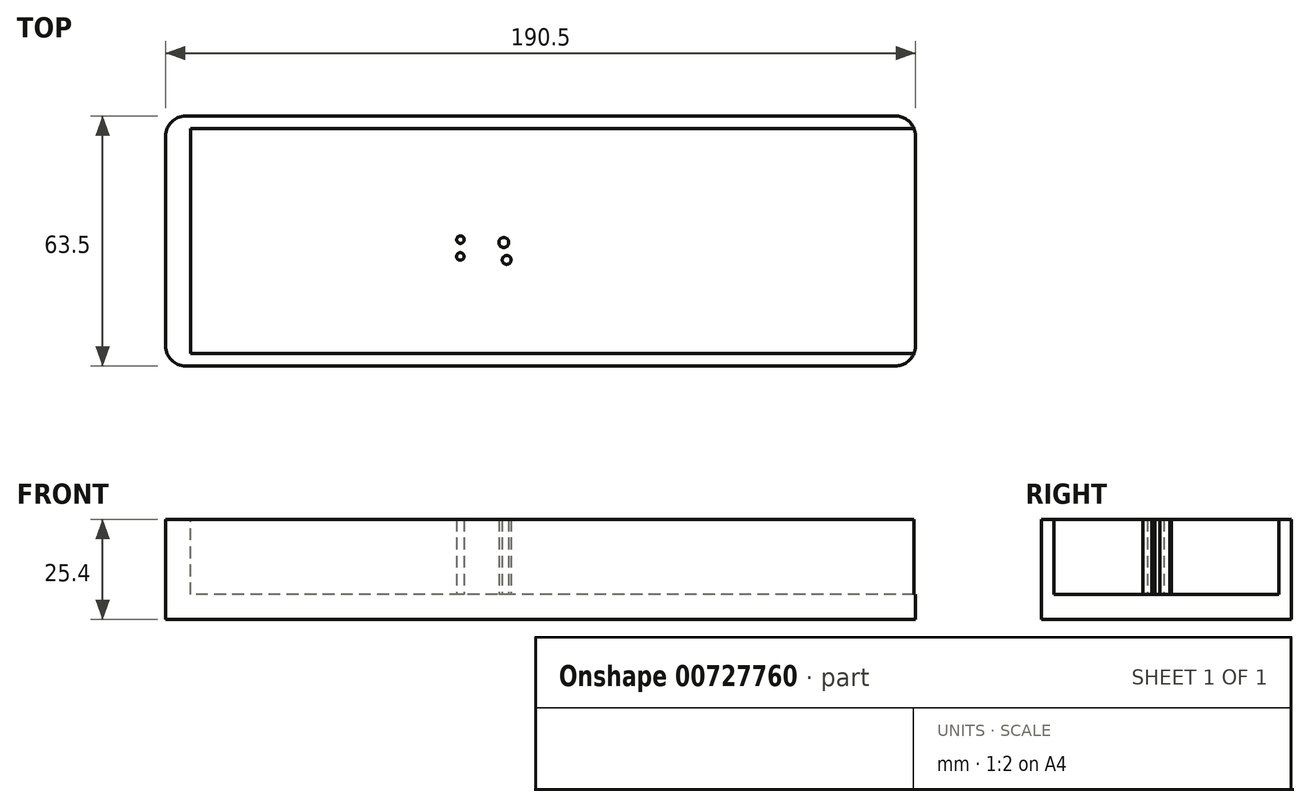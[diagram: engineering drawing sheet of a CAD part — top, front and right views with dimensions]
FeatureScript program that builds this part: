
annotation { "Feature Type Name" : "Feature", "Feature Type Description" : "" }
export const myFeature = defineFeature(function(context is Context, id is Id, definition is map)
    precondition{}
    {
        {
            var Q0;
            Q0=qCreatedBy(makeId("Top.planeOp"),FACE);
            var sketch = newSketch(context, id + "F0", { "sketchPlane" : qUnion([Q0])});
            skLineSegment(sketch, "E0.bottom", {"start": v(95.25, -31.75) * mm, "end": v(-95.25, -31.75) * mm});
            skLineSegment(sketch, "E0.top", {"start": v(95.25, 31.75) * mm, "end": v(-95.25, 31.75) * mm});
            skLineSegment(sketch, "E0.left", {"start": v(95.25, -31.75) * mm, "end": v(95.25, 31.75) * mm});
            skLineSegment(sketch, "E0.right", {"start": v(-95.25, -31.75) * mm, "end": v(-95.25, 31.75) * mm});
            skPoint(sketch, "E0.middle", {"position": v(0, 0) * mm});
            skSolve(sketch);
        }
        {
            var Q0;
            Q0 = qSketchRegion(id + "F0", true);
            extrude(context, id + "F1", {"entities" : qUnion([Q0]), "depth" : 25.4 * mm, "offsetDistance" : 25.4 * mm});
        }
        {
            var Q0;
            Q0=makeQuery(id+"F1.opExtrude","CAP_FACE",FACE,{"disambiguationData":[OSD([sQuery(id+"F0.wireOp",EDGE,"E0.bottom"),sQuery(id+"F0.wireOp",EDGE,"E0.top"),sQuery(id+"F0.wireOp",EDGE,"E0.left"),sQuery(id+"F0.wireOp",EDGE,"E0.right")])],"isStart":false});
            var sketch = newSketch(context, id + "F2", { "sketchPlane" : qUnion([Q0])});
            skLineSegment(sketch, "E1.bottom", {"start": v(95.25, 28.57) * mm, "end": v(-88.9, 28.58) * mm});
            skLineSegment(sketch, "E1.top", {"start": v(95.25, -28.58) * mm, "end": v(-88.9, -28.57) * mm});
            skLineSegment(sketch, "E1.left", {"start": v(95.25, 28.57) * mm, "end": v(95.25, -28.58) * mm});
            skLineSegment(sketch, "E1.right", {"start": v(-88.9, 28.58) * mm, "end": v(-88.9, -28.57) * mm});
            skPoint(sketch, "E1.middle", {"position": v(3.18, 0) * mm});
            skSolve(sketch);
        }
        {
            var Q0;
            Q0 = qSketchRegion(id + "F2", true);
            extrude(context, id + "F3", {"entities" : qUnion([Q0]), "operationType" : NewBodyOperationType.REMOVE, "oppositeDirection" : true, "depth" : 19.05 * mm, "offsetDistance" : 25.4 * mm});
        }
        {
            var Q0;
            Q0=makeQuery(id+"F3.boolean.opBoolean","COPY",FACE,{"derivedFrom":makeQuery(id+"F3.opExtrude","CAP_FACE",FACE,{"disambiguationData":[OSD([sQuery(id+"F2.wireOp",EDGE,"E1.bottom"),sQuery(id+"F2.wireOp",EDGE,"E1.top"),sQuery(id+"F2.wireOp",EDGE,"E1.left"),sQuery(id+"F2.wireOp",EDGE,"E1.right")])],"isStart":false})});
            var sketch = newSketch(context, id + "F4", { "sketchPlane" : qUnion([Q0])});
            skCircle(sketch, "E2", {"center": v(-20.36, 0.36) * mm, "radius": 0.95 * mm});
            skCircle(sketch, "E3", {"center": v(-20.4, -3.91) * mm, "radius": 0.95 * mm});
            skCircle(sketch, "E4", {"center": v(-9.34, -0.37) * mm, "radius": 1.27 * mm});
            skCircle(sketch, "E5", {"center": v(-8.6, -4.8) * mm, "radius": 1.12 * mm});
            skSolve(sketch);
        }
        {
            var Q0;
            Q0 = qSketchRegion(id + "F4", true);
            extrude(context, id + "F5", {"entities" : qUnion([Q0]), "depth" : 19.05 * mm, "offsetDistance" : 25.4 * mm});
        }
        {
            var Q0;
            Q0=makeQuery(id+"F1.opExtrude","SWEPT_EDGE",EDGE,{"disambiguationData":[OSD([sQuery(id+"F0.wireOp",EDGE,"E0.bottom"),sQuery(id+"F0.wireOp",EDGE,"E0.right")])]});
            var Q1;
            Q1=makeQuery(id+"F1.opExtrude","SWEPT_EDGE",EDGE,{"disambiguationData":[OSD([sQuery(id+"F0.wireOp",EDGE,"E0.top"),sQuery(id+"F0.wireOp",EDGE,"E0.right")])]});
            var Q2;
            Q2=makeQuery(id+"F1.opExtrude","SWEPT_EDGE",EDGE,{"disambiguationData":[OSD([sQuery(id+"F0.wireOp",EDGE,"E0.top"),sQuery(id+"F0.wireOp",EDGE,"E0.left")])]});
            var Q3;
            Q3=makeQuery(id+"F1.opExtrude","SWEPT_EDGE",EDGE,{"disambiguationData":[OSD([sQuery(id+"F0.wireOp",EDGE,"E0.bottom"),sQuery(id+"F0.wireOp",EDGE,"E0.left")])]});
            fillet(context, id + "F6", {"entities" : qUnion([Q0, Q1, Q2, Q3]), "radius" : 5.08 * mm, "tangentPropagation" : true, "allowEdgeOverflow" : false});
        }
    });
